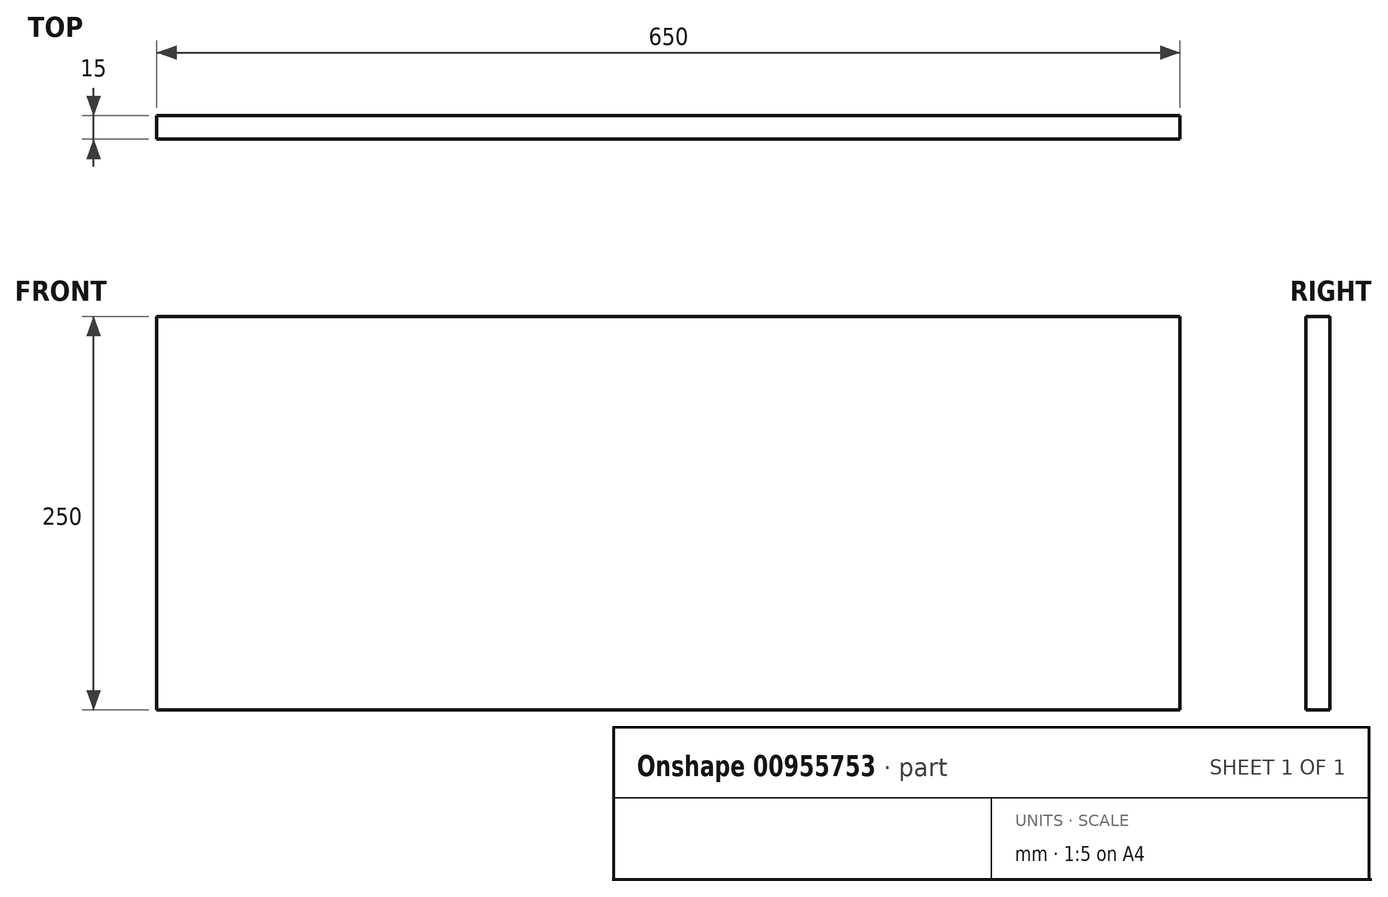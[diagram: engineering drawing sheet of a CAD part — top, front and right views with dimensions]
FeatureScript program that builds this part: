
annotation { "Feature Type Name" : "Feature", "Feature Type Description" : "" }
export const myFeature = defineFeature(function(context is Context, id is Id, definition is map)
    precondition{}
    {
        {
            var Q0;
            Q0=qCreatedBy(makeId("Front.planeOp"),FACE);
            var sketch = newSketch(context, id + "F0", { "sketchPlane" : qUnion([Q0])});
            skLineSegment(sketch, "E0.bottom", {"start": v(0, 0) * mm, "end": v(650, 0) * mm});
            skLineSegment(sketch, "E0.top", {"start": v(0, -250) * mm, "end": v(650, -250) * mm});
            skLineSegment(sketch, "E0.left", {"start": v(0, 0) * mm, "end": v(0, -250) * mm});
            skLineSegment(sketch, "E0.right", {"start": v(650, 0) * mm, "end": v(650, -250) * mm});
            skSolve(sketch);
        }
        {
            var Q0;
            Q0 = qSketchRegion(id + "F0", true);
            extrude(context, id + "F1", {"entities" : qUnion([Q0]), "depth" : 15 * mm, "offsetDistance" : 25 * mm});
        }
    });
